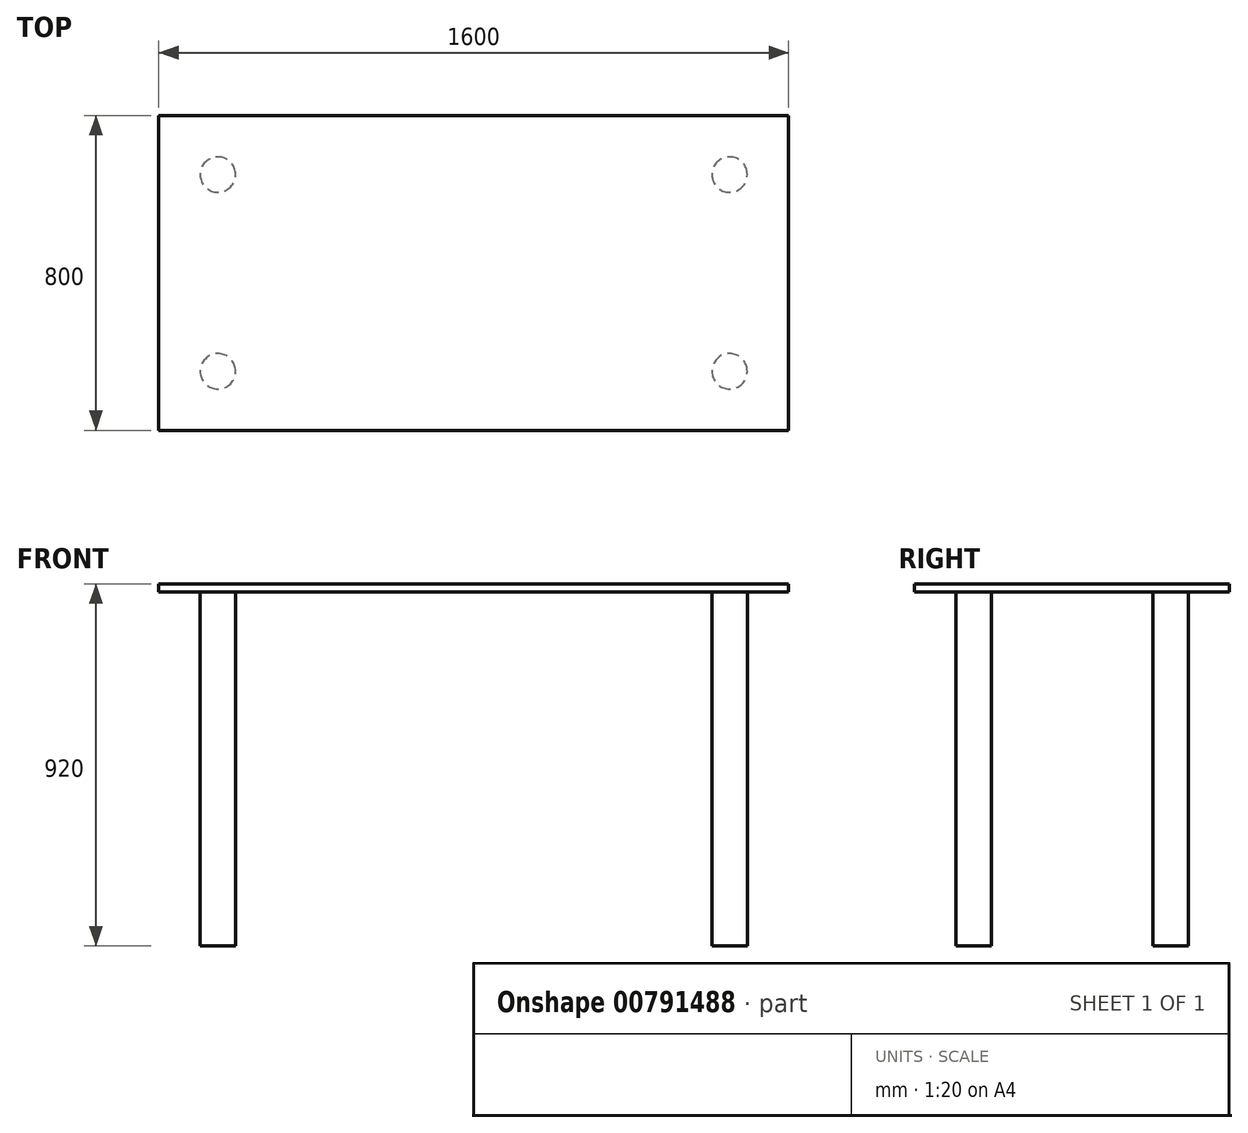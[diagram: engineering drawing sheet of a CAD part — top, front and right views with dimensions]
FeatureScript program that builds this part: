
annotation { "Feature Type Name" : "Feature", "Feature Type Description" : "" }
export const myFeature = defineFeature(function(context is Context, id is Id, definition is map)
    precondition{}
    {
        {
            var Q0;
            Q0=qCreatedBy(makeId("Top.planeOp"),FACE);
            var sketch = newSketch(context, id + "F0", { "sketchPlane" : qUnion([Q0])});
            skLineSegment(sketch, "E0.bottom", {"start": v(800, -400) * mm, "end": v(-800, -400) * mm});
            skLineSegment(sketch, "E0.top", {"start": v(800, 400) * mm, "end": v(-800, 400) * mm});
            skLineSegment(sketch, "E0.left", {"start": v(800, -400) * mm, "end": v(800, 400) * mm});
            skLineSegment(sketch, "E0.right", {"start": v(-800, -400) * mm, "end": v(-800, 400) * mm});
            skPoint(sketch, "E0.middle", {"position": v(0, 0) * mm});
            skSolve(sketch);
        }
        {
            var Q0;
            Q0 = qSketchRegion(id + "F0", true);
            var Q1;
            Q1=makeQuery(id+"F0.imprint","IMPRINT",FACE,{"disambiguationData":[TD([[makeQuery(id+"F0.imprint","IMPRINT",EDGE,{"derivedFrom":sQuery(id+"F0.wireOp",EDGE,"E0.bottom")}),-1.0]])]});
            extrude(context, id + "F1", {"entities" : qUnion([Q0, Q1]), "depth" : 20 * mm, "offsetDistance" : 25 * mm});
        }
        {
            var Q0;
            Q0=makeQuery(id+"F1.opExtrude","CAP_FACE",FACE,{"disambiguationData":[OSD([sQuery(id+"F0.wireOp",EDGE,"E0.bottom"),sQuery(id+"F0.wireOp",EDGE,"E0.top"),sQuery(id+"F0.wireOp",EDGE,"E0.left"),sQuery(id+"F0.wireOp",EDGE,"E0.right")])],"isStart":false});
            var sketch = newSketch(context, id + "F2", { "sketchPlane" : qUnion([Q0])});
            skLineSegment(sketch, "E1", {"start": v(0, -400) * mm, "end": v(0, 400) * mm, "construction": true});
            skLineSegment(sketch, "E2", {"start": v(800, 0) * mm, "end": v(-800, 0) * mm, "construction": true});
            skLineSegment(sketch, "E3", {"start": v(-650, 400) * mm, "end": v(-650, 250) * mm, "construction": true});
            skLineSegment(sketch, "E4", {"start": v(-650, 250) * mm, "end": v(-800, 250) * mm, "construction": true});
            skCircle(sketch, "E5", {"center": v(-650, 250) * mm, "radius": 45 * mm});
            skCircle(sketch, "E6.MirrorC", {"center": v(650, 250) * mm, "radius": 45 * mm});
            skCircle(sketch, "E7.MirrorC", {"center": v(-650, -250) * mm, "radius": 45 * mm});
            skCircle(sketch, "E8.MirrorC", {"center": v(650, -250) * mm, "radius": 45 * mm});
            skSolve(sketch);
        }
        {
            var Q0;
            Q0 = qSketchRegion(id + "F2", true);
            extrude(context, id + "F3", {"entities" : qUnion([Q0]), "operationType" : NewBodyOperationType.ADD, "depth" : 900 * mm, "offsetDistance" : 25 * mm});
        }
        {
            var Q0;
            Q0=makeQuery(id+"F1.opExtrude","SWEPT_BODY",BODY,{"disambiguationData":[OSD([sQuery(id+"F0.wireOp",EDGE,"E0.bottom"),sQuery(id+"F0.wireOp",EDGE,"E0.top"),sQuery(id+"F0.wireOp",EDGE,"E0.left"),sQuery(id+"F0.wireOp",EDGE,"E0.right")])]});
            var Q1;
            Q1=makeQuery(id+"F3.opExtrude","SWEPT_BODY",BODY,{"disambiguationData":[OSD([sQuery(id+"F2.wireOp",EDGE,"E7.MirrorC")])]});
            var Q2;
            Q2=makeQuery(id+"F3.opExtrude","SWEPT_BODY",BODY,{"disambiguationData":[OSD([sQuery(id+"F2.wireOp",EDGE,"E8.MirrorC")])]});
            var Q3;
            Q3=makeQuery(id+"F3.opExtrude","SWEPT_BODY",BODY,{"disambiguationData":[OSD([sQuery(id+"F2.wireOp",EDGE,"E5")])]});
            var Q4;
            Q4=makeQuery(id+"F3.opExtrude","SWEPT_BODY",BODY,{"disambiguationData":[OSD([sQuery(id+"F2.wireOp",EDGE,"E6.MirrorC")])]});
            var Q5;
            Q5=makeQuery(id+"F1.opExtrude","CAP_EDGE",EDGE,{"disambiguationData":[OSD([sQuery(id+"F0.wireOp",EDGE,"E0.bottom")])],"isStart":true});
            var Q6;
            Q6=makeQuery(id+"F1.opExtrude","CAP_EDGE",EDGE,{"disambiguationData":[OSD([sQuery(id+"F0.wireOp",EDGE,"E0.bottom")])],"isStart":false});
            transform(context, id + "F4", {"entities" : qUnion([Q0, Q1, Q2, Q3, Q4]), "transformType" : TransformType.ROTATION, "transformAxis" : qUnion([Q6]), "angle" : 180 * degree, "makeCopy" : false});
        }
    });
